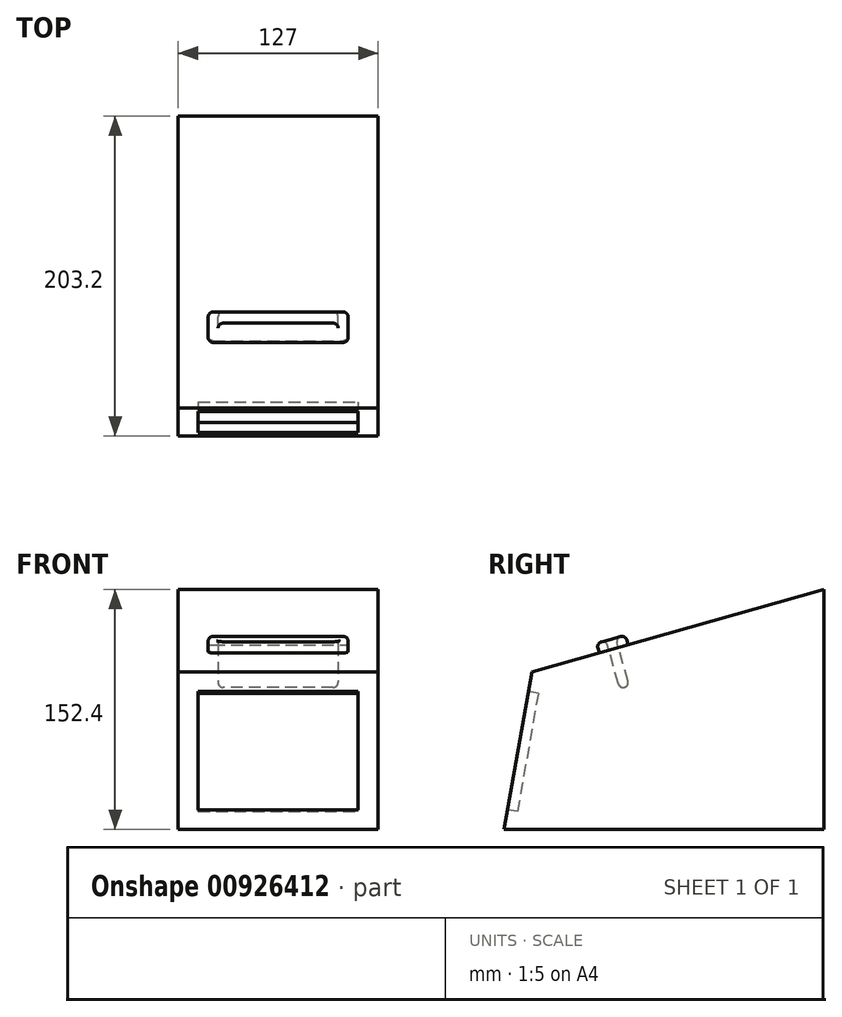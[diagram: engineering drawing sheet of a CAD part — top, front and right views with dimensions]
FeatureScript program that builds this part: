
annotation { "Feature Type Name" : "Feature", "Feature Type Description" : "" }
export const myFeature = defineFeature(function(context is Context, id is Id, definition is map)
    precondition{}
    {
        {
            var Q0;
            Q0=qCreatedBy(makeId("Right.planeOp"),FACE);
            var sketch = newSketch(context, id + "F0", { "sketchPlane" : qUnion([Q0])});
            skLineSegment(sketch, "E0", {"start": v(-82.78, 10.24) * mm, "end": v(120.42, 10.24) * mm});
            skLineSegment(sketch, "E1", {"start": v(-82.78, 10.24) * mm, "end": v(-65.14, 110.3) * mm});
            skLineSegment(sketch, "E2", {"start": v(120.42, 10.24) * mm, "end": v(120.42, 162.64) * mm});
            skLineSegment(sketch, "E3", {"start": v(120.42, 162.64) * mm, "end": v(-65.14, 110.3) * mm});
            skSolve(sketch);
        }
        {
            var Q0;
            Q0=makeQuery(id+"F0.imprint","IMPRINT",FACE,{"disambiguationData":[TD([[makeQuery(id+"F0.imprint","IMPRINT",EDGE,{"derivedFrom":sQuery(id+"F0.wireOp",EDGE,"E0")}),1.0]])]});
            extrude(context, id + "F1", {"entities" : qUnion([Q0]), "depth" : 127 * mm, "offsetDistance" : 25.4 * mm});
        }
        {
            var Q0;
            Q0=makeQuery(id+"F1.opExtrude","SWEPT_FACE",FACE,{"disambiguationData":[OSD([sQuery(id+"F0.wireOp",EDGE,"E1")])]});
            var sketch = newSketch(context, id + "F2", { "sketchPlane" : qUnion([Q0])});
            skLineSegment(sketch, "E4.bottom", {"start": v(0, 97.31) * mm, "end": v(127, 97.31) * mm});
            skLineSegment(sketch, "E4.left", {"start": v(0, 97.31) * mm, "end": v(0, -4.29) * mm});
            skLineSegment(sketch, "E5", {"start": v(0, 97.31) * mm, "end": v(12.7, 97.31) * mm});
            skLineSegment(sketch, "E6", {"start": v(12.7, 97.31) * mm, "end": v(12.7, 84.61) * mm});
            skLineSegment(sketch, "E7", {"start": v(127, -4.29) * mm, "end": v(114.3, -4.29) * mm});
            skLineSegment(sketch, "E8", {"start": v(127, -4.29) * mm, "end": v(127, 8.41) * mm});
            skLineSegment(sketch, "E9", {"start": v(127, 8.41) * mm, "end": v(114.3, 8.41) * mm});
            skLineSegment(sketch, "E10.bottom", {"start": v(12.7, 84.61) * mm, "end": v(114.3, 84.61) * mm});
            skLineSegment(sketch, "E10.top", {"start": v(12.7, 8.41) * mm, "end": v(114.3, 8.41) * mm});
            skLineSegment(sketch, "E10.left", {"start": v(12.7, 84.61) * mm, "end": v(12.7, 8.41) * mm});
            skLineSegment(sketch, "E10.right", {"start": v(114.3, 84.61) * mm, "end": v(114.3, 8.41) * mm});
            skSolve(sketch);
        }
        {
            var Q0;
            Q0=makeQuery(id+"F2.imprint","IMPRINT",FACE,{"disambiguationData":[TD([[makeQuery(id+"F2.imprint","IMPRINT",EDGE,{"derivedFrom":sQuery(id+"F2.wireOp",EDGE,"E10.bottom")}),-1.0]])]});
            extrude(context, id + "F3", {"entities" : qUnion([Q0]), "operationType" : NewBodyOperationType.REMOVE, "oppositeDirection" : true, "depth" : 6.35 * mm, "offsetDistance" : 25.4 * mm});
        }
        {
            var Q0;
            Q0=makeQuery(id+"F1.opExtrude","SWEPT_FACE",FACE,{"disambiguationData":[OSD([sQuery(id+"F0.wireOp",EDGE,"E3")])]});
            var sketch = newSketch(context, id + "F4", { "sketchPlane" : qUnion([Q0])});
            skLineSegment(sketch, "E11", {"start": v(0, -32.75) * mm, "end": v(0, 18.05) * mm});
            skLineSegment(sketch, "E12", {"start": v(0, 18.05) * mm, "end": v(25.4, 18.05) * mm});
            skLineSegment(sketch, "E13", {"start": v(25.4, 18.05) * mm, "end": v(101.6, 18.05) * mm});
            skLineSegment(sketch, "E14", {"start": v(25.4, 18.05) * mm, "end": v(25.4, 24.4) * mm});
            skLineSegment(sketch, "E15.bottom", {"start": v(25.4, 24.4) * mm, "end": v(101.6, 24.4) * mm});
            skLineSegment(sketch, "E15.left", {"start": v(25.4, 24.4) * mm, "end": v(25.4, 18.05) * mm});
            skLineSegment(sketch, "E15.right", {"start": v(101.6, 24.4) * mm, "end": v(101.6, 18.05) * mm});
            skSolve(sketch);
        }
        {
            var Q0;
            Q0=makeQuery(id+"F4.imprint","IMPRINT",FACE,{"disambiguationData":[TD([[makeQuery(id+"F4.imprint","IMPRINT",EDGE,{"derivedFrom":sQuery(id+"F4.wireOp",EDGE,"E15.bottom")}),-1.0]])]});
            extrude(context, id + "F5", {"entities" : qUnion([Q0]), "operationType" : NewBodyOperationType.REMOVE, "oppositeDirection" : true, "depth" : 25.4 * mm, "offsetDistance" : 25.4 * mm});
        }
        {
            var Q0;
            Q0=makeQuery(id+"F1.opExtrude","SWEPT_FACE",FACE,{"disambiguationData":[OSD([sQuery(id+"F0.wireOp",EDGE,"E3")])]});
            var sketch = newSketch(context, id + "F6", { "sketchPlane" : qUnion([Q0])});
            skLineSegment(sketch, "E16.bottom", {"start": v(25.4, 24.4) * mm, "end": v(101.6, 24.4) * mm});
            skLineSegment(sketch, "E16.top", {"start": v(25.4, 18.05) * mm, "end": v(101.6, 18.05) * mm});
            skLineSegment(sketch, "E16.left", {"start": v(25.4, 24.4) * mm, "end": v(25.4, 18.05) * mm});
            skLineSegment(sketch, "E16.right", {"start": v(101.6, 24.4) * mm, "end": v(101.6, 18.05) * mm});
            skLineSegment(sketch, "E17", {"start": v(25.4, 24.4) * mm, "end": v(25.4, 30.75) * mm});
            skLineSegment(sketch, "E18", {"start": v(25.4, 30.75) * mm, "end": v(19.05, 30.75) * mm});
            skLineSegment(sketch, "E19", {"start": v(101.6, 18.05) * mm, "end": v(101.6, 11.7) * mm});
            skLineSegment(sketch, "E20", {"start": v(101.6, 11.7) * mm, "end": v(107.95, 11.7) * mm});
            skLineSegment(sketch, "E21.bottom", {"start": v(19.05, 30.75) * mm, "end": v(107.95, 30.75) * mm});
            skLineSegment(sketch, "E21.top", {"start": v(19.05, 11.7) * mm, "end": v(107.95, 11.7) * mm});
            skLineSegment(sketch, "E21.left", {"start": v(19.05, 30.75) * mm, "end": v(19.05, 11.7) * mm});
            skLineSegment(sketch, "E21.right", {"start": v(107.95, 30.75) * mm, "end": v(107.95, 11.7) * mm});
            skSolve(sketch);
        }
        {
            var Q0;
            Q0=makeQuery(id+"F6.imprint","IMPRINT",FACE,{"disambiguationData":[TD([[makeQuery(id+"F6.imprint","IMPRINT",EDGE,{"derivedFrom":sQuery(id+"F6.wireOp",EDGE,"E16.bottom")}),1.0]])]});
            var Q1;
            Q1=makeQuery(id+"F6.imprint","IMPRINT",FACE,{"disambiguationData":[TD([[makeQuery(id+"F6.imprint","IMPRINT",EDGE,{"derivedFrom":sQuery(id+"F6.wireOp",EDGE,"E16.top")}),-1.0]])]});
            extrude(context, id + "F7", {"entities" : qUnion([Q0, Q1]), "operationType" : NewBodyOperationType.ADD, "depth" : 6.35 * mm, "offsetDistance" : 25.4 * mm});
        }
        {
            var Q0;
            Q0=makeQuery(id+"F7.opExtrude","CAP_EDGE",EDGE,{"disambiguationData":[OSD([sQuery(id+"F6.wireOp",EDGE,"E21.top")])],"isStart":true});
            var Q1;
            Q1=makeQuery(id+"F7.opExtrude","CAP_EDGE",EDGE,{"disambiguationData":[OSD([sQuery(id+"F6.wireOp",EDGE,"E21.right")])],"isStart":true});
            var Q2;
            Q2=makeQuery(id+"F7.opExtrude","CAP_EDGE",EDGE,{"disambiguationData":[OSD([sQuery(id+"F6.wireOp",EDGE,"E21.bottom")])],"isStart":true});
            var Q3;
            Q3=makeQuery(id+"F7.opExtrude","CAP_EDGE",EDGE,{"disambiguationData":[OSD([sQuery(id+"F6.wireOp",EDGE,"E21.left")])],"isStart":true});
            var Q4;
            Q4=makeQuery(id+"F7.opExtrude","CAP_EDGE",EDGE,{"disambiguationData":[OSD([sQuery(id+"F6.wireOp",EDGE,"E21.top")])],"isStart":false});
            var Q5;
            Q5=makeQuery(id+"F7.opExtrude","CAP_EDGE",EDGE,{"disambiguationData":[OSD([sQuery(id+"F6.wireOp",EDGE,"E21.right")])],"isStart":false});
            var Q6;
            Q6=makeQuery(id+"F7.opExtrude","CAP_EDGE",EDGE,{"disambiguationData":[OSD([sQuery(id+"F6.wireOp",EDGE,"E21.bottom")])],"isStart":false});
            var Q7;
            Q7=makeQuery(id+"F7.opExtrude","CAP_EDGE",EDGE,{"disambiguationData":[OSD([sQuery(id+"F6.wireOp",EDGE,"E21.left")])],"isStart":false});
            var Q8;
            Q8=makeQuery(id+"F7.opExtrude","SWEPT_EDGE",EDGE,{"disambiguationData":[OSD([sQuery(id+"F6.wireOp",EDGE,"E21.top"),sQuery(id+"F6.wireOp",EDGE,"E21.left")])]});
            var Q9;
            Q9=makeQuery(id+"F7.opExtrude","SWEPT_EDGE",EDGE,{"disambiguationData":[OSD([sQuery(id+"F6.wireOp",EDGE,"E21.bottom"),sQuery(id+"F6.wireOp",EDGE,"E21.left")])]});
            var Q10;
            Q10=makeQuery(id+"F7.opExtrude","SWEPT_EDGE",EDGE,{"disambiguationData":[OSD([sQuery(id+"F6.wireOp",EDGE,"E21.top"),sQuery(id+"F6.wireOp",EDGE,"E21.right")])]});
            var Q11;
            Q11=makeQuery(id+"F7.opExtrude","SWEPT_EDGE",EDGE,{"disambiguationData":[OSD([sQuery(id+"F6.wireOp",EDGE,"E21.bottom"),sQuery(id+"F6.wireOp",EDGE,"E21.right")])]});
            var Q12;
            Q12=makeQuery(id+"F7.opExtrude","CAP_EDGE",EDGE,{"disambiguationData":[OSD([sQuery(id+"F6.wireOp",EDGE,"E16.bottom")])],"isStart":false});
            var Q13;
            Q13=makeQuery(id+"F7.opExtrude","CAP_EDGE",EDGE,{"disambiguationData":[OSD([sQuery(id+"F6.wireOp",EDGE,"E16.right")])],"isStart":false});
            var Q14;
            Q14=makeQuery(id+"F7.opExtrude","CAP_EDGE",EDGE,{"disambiguationData":[OSD([sQuery(id+"F6.wireOp",EDGE,"E16.top")])],"isStart":false});
            var Q15;
            Q15=makeQuery(id+"F7.opExtrude","CAP_EDGE",EDGE,{"disambiguationData":[OSD([sQuery(id+"F6.wireOp",EDGE,"E16.left")])],"isStart":false});
            var Q16;
            Q16=makeQuery(id+"F7.boolean.opBoolean","MERGE",EDGE,{"derivedFrom":[makeQuery(id+"F5.boolean.opBoolean","COPY",EDGE,{"derivedFrom":makeQuery(id+"F5.opExtrude","SWEPT_EDGE",EDGE,{"disambiguationData":[OSD([sQuery(id+"F4.wireOp",EDGE,"E13"),sQuery(id+"F4.wireOp",EDGE,"E15.left")])]})}),makeQuery(id+"F7.opExtrude","SWEPT_EDGE",EDGE,{"disambiguationData":[OSD([sQuery(id+"F6.wireOp",EDGE,"E16.top"),sQuery(id+"F6.wireOp",EDGE,"E16.left")])]})]});
            var Q17;
            Q17=makeQuery(id+"F7.boolean.opBoolean","MERGE",EDGE,{"derivedFrom":[makeQuery(id+"F5.boolean.opBoolean","COPY",EDGE,{"derivedFrom":makeQuery(id+"F5.opExtrude","SWEPT_EDGE",EDGE,{"disambiguationData":[OSD([sQuery(id+"F4.wireOp",EDGE,"E15.bottom"),sQuery(id+"F4.wireOp",EDGE,"E15.left")])]})}),makeQuery(id+"F7.opExtrude","SWEPT_EDGE",EDGE,{"disambiguationData":[OSD([sQuery(id+"F6.wireOp",EDGE,"E16.bottom"),sQuery(id+"F6.wireOp",EDGE,"E16.left"),sQuery(id+"F6.wireOp",EDGE,"E17")])]})]});
            var Q18;
            Q18=makeQuery(id+"F7.boolean.opBoolean","MERGE",EDGE,{"derivedFrom":[makeQuery(id+"F5.boolean.opBoolean","COPY",EDGE,{"derivedFrom":makeQuery(id+"F5.opExtrude","SWEPT_EDGE",EDGE,{"disambiguationData":[OSD([sQuery(id+"F4.wireOp",EDGE,"E15.bottom"),sQuery(id+"F4.wireOp",EDGE,"E15.right")])]})}),makeQuery(id+"F7.opExtrude","SWEPT_EDGE",EDGE,{"disambiguationData":[OSD([sQuery(id+"F6.wireOp",EDGE,"E16.bottom"),sQuery(id+"F6.wireOp",EDGE,"E16.right")])]})]});
            var Q19;
            Q19=makeQuery(id+"F7.boolean.opBoolean","MERGE",EDGE,{"derivedFrom":[makeQuery(id+"F5.boolean.opBoolean","COPY",EDGE,{"derivedFrom":makeQuery(id+"F5.opExtrude","SWEPT_EDGE",EDGE,{"disambiguationData":[OSD([sQuery(id+"F4.wireOp",EDGE,"E13"),sQuery(id+"F4.wireOp",EDGE,"E15.right")])]})}),makeQuery(id+"F7.opExtrude","SWEPT_EDGE",EDGE,{"disambiguationData":[OSD([sQuery(id+"F6.wireOp",EDGE,"E16.top"),sQuery(id+"F6.wireOp",EDGE,"E16.right"),sQuery(id+"F6.wireOp",EDGE,"E19")])]})]});
            fillet(context, id + "F8", {"entities" : qUnion([Q0, Q1, Q2, Q3, Q4, Q5, Q6, Q7, Q8, Q9, Q10, Q11, Q12, Q13, Q14, Q15, Q16, Q17, Q18, Q19]), "radius" : 3.17 * mm, "tangentPropagation" : true, "allowEdgeOverflow" : false});
        }
        {
            var Q0;
            Q0=makeQuery(id+"F5.boolean.opBoolean","COPY",EDGE,{"derivedFrom":makeQuery(id+"F5.opExtrude","CAP_EDGE",EDGE,{"disambiguationData":[OSD([sQuery(id+"F4.wireOp",EDGE,"E15.bottom")])],"isStart":false})});
            fillet(context, id + "F9", {"entities" : qUnion([Q0]), "radius" : 3.17 * mm, "tangentPropagation" : true, "allowEdgeOverflow" : false});
        }
    });
